# Revit family: CLS
name_source: partatom
category: Lighting Fixtures
revit_build: Autodesk Revit MEP 2012 (Build: 20110309_2315(x64)
units: mm (PartAtom-declared; Revit-internal decimal feet)

## types (2) — shared parameters
Apparent Load = 5 VA
Backbox = Hubbell - White
Color Filter = 16777215
Connector Description = Lighting Connector
Default Elevation = 48.000"
Description = The CLS Series offers bright and even LED “EXIT” or “STAIRS” glass panel illumination with Red letters, white LED's and a 20 gauge, durable steel housing.
Dimming Lamp Color Temperature Shift = <None>
Emit Shape Visible in Rendering = No
Emit from Rectangle Width = 10.717"
Family = Outdoor Emergency Lighting
Glass = Hubbell - light Glass
Lamp = LED
Lettering = Hubbell - Red Glass
Load Classification = Other
Manufacturer = Dual-Lite
Manufacturer Fax = (864)-678-1415
Model = CLS
Mounting = Ceiling Mount
Photometric Web File = generic
Product Documentation Link = http://cdn.dual-lite.com
Product Page URL = http://www.dual-lite.com
URL = http://www.dual-lite.com
Wattage Comments = 5 W

## per-type parameters (varying)
| type | Depth | Emit from Rectangle Length | Letters | Tilt Angle | Voltage | Width |
| CLS - EXIT | 11.187" | 12.375" | Lettering : EXIT | 90.00° | 120 V | 12.375" |
| CLS - STAIRS | 11.340" | 13.875" | Lettering : STAIRS | 60.00° | 0 V | 13.875" |

## geometry (parser evidence)
native form markers: Sweep x4
no freeform markers — native parametric forms only
